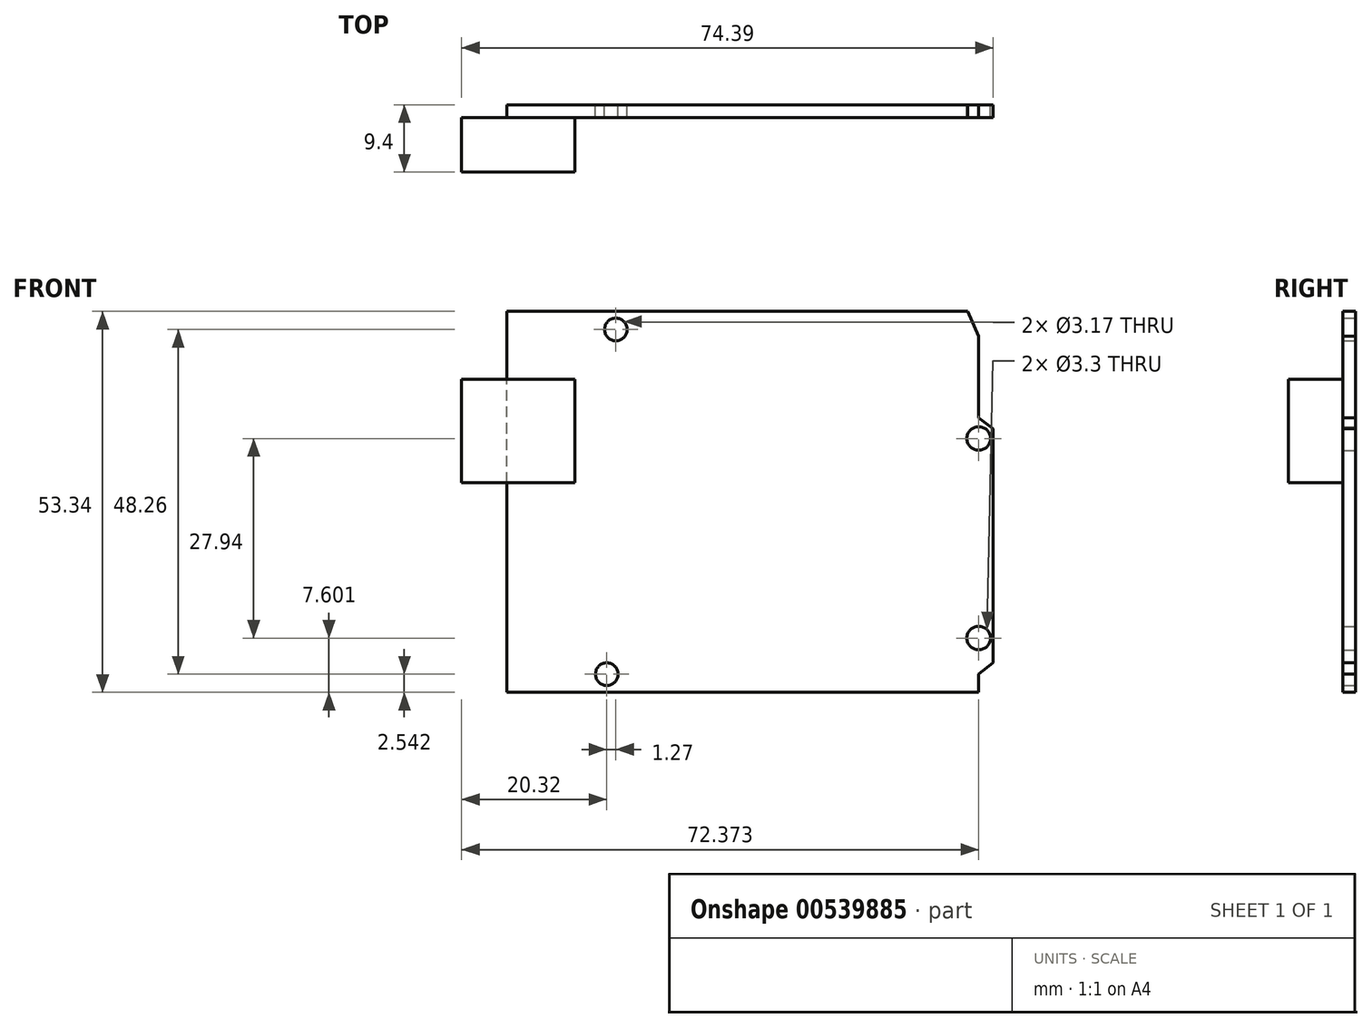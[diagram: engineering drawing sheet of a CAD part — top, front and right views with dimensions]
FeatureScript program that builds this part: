
annotation { "Feature Type Name" : "Feature", "Feature Type Description" : "" }
export const myFeature = defineFeature(function(context is Context, id is Id, definition is map)
    precondition{}
    {
        {
            var Q0;
            Q0=qCreatedBy(makeId("Front.planeOp"),FACE);
            var sketch = newSketch(context, id + "F0", { "sketchPlane" : qUnion([Q0])});
            skLineSegment(sketch, "E0", {"start": v(-50.8, -29.33) * mm, "end": v(-50.8, 24.01) * mm});
            skLineSegment(sketch, "E1", {"start": v(-50.8, -29.33) * mm, "end": v(15.24, -29.33) * mm});
            skLineSegment(sketch, "E2", {"start": v(15.24, -29.33) * mm, "end": v(15.24, -26.79) * mm});
            skLineSegment(sketch, "E3", {"start": v(15.24, -26.79) * mm, "end": v(17.24, -25.22) * mm});
            skLineSegment(sketch, "E4", {"start": v(17.24, -25.22) * mm, "end": v(17.24, 7.55) * mm});
            skLineSegment(sketch, "E5", {"start": v(17.24, 7.55) * mm, "end": v(15.24, 9.12) * mm});
            skLineSegment(sketch, "E6", {"start": v(-50.8, 24.01) * mm, "end": v(13.72, 24.01) * mm});
            skLineSegment(sketch, "E7", {"start": v(15.24, 9.12) * mm, "end": v(15.24, 20.55) * mm});
            skLineSegment(sketch, "E8", {"start": v(15.24, 20.55) * mm, "end": v(13.72, 24.01) * mm});
            skLineSegment(sketch, "E9", {"start": v(-50.8, 24.01) * mm, "end": v(-35.56, 24.01) * mm});
            skLineSegment(sketch, "E10", {"start": v(-35.56, 24.01) * mm, "end": v(-35.56, 21.47) * mm});
            skCircle(sketch, "E11", {"center": v(-35.56, 21.47) * mm, "radius": 1.59 * mm});
            skLineSegment(sketch, "E12", {"start": v(-50.8, -29.33) * mm, "end": v(-36.83, -29.33) * mm});
            skLineSegment(sketch, "E13", {"start": v(-36.83, -29.33) * mm, "end": v(-36.83, -26.79) * mm});
            skCircle(sketch, "E14", {"center": v(-36.83, -26.79) * mm, "radius": 1.59 * mm});
            skLineSegment(sketch, "E15", {"start": v(-50.8, -29.33) * mm, "end": v(0, -29.33) * mm});
            skSolve(sketch);
        }
        {
            var Q0;
            {var subQ0=sQuery(id+"F0.wireOp",EDGE,"E0");Q0=makeQuery(id+"F0.imprint","IMPRINT",FACE,{"disambiguationData":[TD([[makeQuery(id+"F0.imprint","IMPRINT",EDGE,{"derivedFrom":subQ0}),-1.0]])]});}
            var sketch = newSketch(context, id + "F1", { "sketchPlane" : qUnion([Q0])});
            skLineSegment(sketch, "E16", {"start": v(15.22, -29.35) * mm, "end": v(15.22, -21.73) * mm});
            skCircle(sketch, "E17", {"center": v(15.22, -21.73) * mm, "radius": 1.59 * mm});
            skLineSegment(sketch, "E18", {"start": v(15.22, -29.35) * mm, "end": v(15.22, 6.21) * mm});
            skCircle(sketch, "E19", {"center": v(15.22, 6.21) * mm, "radius": 1.59 * mm});
            skSolve(sketch);
        }
        {
            var Q0;
            {var subQ0=sQuery(id+"F0.wireOp",EDGE,"E0");Q0=makeQuery(id+"F0.imprint","IMPRINT",FACE,{"disambiguationData":[TD([[makeQuery(id+"F0.imprint","IMPRINT",EDGE,{"derivedFrom":subQ0}),-1.0]])]});}
            extrude(context, id + "F2", {"entities" : qUnion([Q0]), "depth" : 1.78 * mm, "offsetDistance" : 25.4 * mm});
        }
        {
            var Q0;
            Q0=sQuery(id+"F1.wireOp",VERTEX,"E17.center");
            var Q1;
            Q1=sQuery(id+"F1.wireOp",VERTEX,"E19.center");
            var Q2;
            Q2=makeQuery(id+"F2.opExtrude","SWEPT_BODY",BODY,{"disambiguationData":[OSD([sQuery(id+"F0.wireOp",EDGE,"E0"),sQuery(id+"F0.wireOp",EDGE,"E2"),sQuery(id+"F0.wireOp",EDGE,"E3"),sQuery(id+"F0.wireOp",EDGE,"E4"),sQuery(id+"F0.wireOp",EDGE,"E5"),sQuery(id+"F0.wireOp",EDGE,"E6"),sQuery(id+"F0.wireOp",EDGE,"E7"),sQuery(id+"F0.wireOp",EDGE,"E8"),sQuery(id+"F0.wireOp",EDGE,"E9"),sQuery(id+"F0.wireOp",EDGE,"E11"),sQuery(id+"F0.wireOp",EDGE,"E14"),sQuery(id+"F0.wireOp",EDGE,"E1")])]});
            hole(context, id + "F3", {"style" : HoleStyle.SIMPLE, "endStyle" : HoleEndStyle.THROUGH, "oppositeDirection" : true, "holeDiameter" : 3.3 * mm, "isTappedThrough" : true, "tappedDepth" : 12.7 * mm, "tapClearance" : 3, "locations" : qUnion([Q0, Q1]), "scope" : qUnion([Q2])});
        }
        {
            var Q0;
            Q0=makeQuery(id+"F2.opExtrude","CAP_FACE",FACE,{"disambiguationData":[OSD([sQuery(id+"F0.wireOp",EDGE,"E0"),sQuery(id+"F0.wireOp",EDGE,"E2"),sQuery(id+"F0.wireOp",EDGE,"E3"),sQuery(id+"F0.wireOp",EDGE,"E4"),sQuery(id+"F0.wireOp",EDGE,"E5"),sQuery(id+"F0.wireOp",EDGE,"E6"),sQuery(id+"F0.wireOp",EDGE,"E7"),sQuery(id+"F0.wireOp",EDGE,"E8"),sQuery(id+"F0.wireOp",EDGE,"E9"),sQuery(id+"F0.wireOp",EDGE,"E11"),sQuery(id+"F0.wireOp",EDGE,"E14"),sQuery(id+"F0.wireOp",EDGE,"E1")])],"isStart":false});
            var sketch = newSketch(context, id + "F4", { "sketchPlane" : qUnion([Q0])});
            skLineSegment(sketch, "E20", {"start": v(-50.8, -29.33) * mm, "end": v(-50.8, 14.49) * mm});
            skLineSegment(sketch, "E21", {"start": v(-50.8, 14.49) * mm, "end": v(-57.15, 14.49) * mm});
            skLineSegment(sketch, "E22", {"start": v(-57.15, 14.49) * mm, "end": v(-57.15, 0) * mm});
            skLineSegment(sketch, "E23", {"start": v(-50.8, 14.49) * mm, "end": v(-41.28, 14.49) * mm});
            skLineSegment(sketch, "E24", {"start": v(-41.28, 14.49) * mm, "end": v(-41.28, 0) * mm});
            skLineSegment(sketch, "E25", {"start": v(-41.28, 0) * mm, "end": v(-57.15, 0) * mm});
            skLineSegment(sketch, "E26", {"start": v(-50.8, -29.33) * mm, "end": v(-50.8, -26.15) * mm});
            skLineSegment(sketch, "E27", {"start": v(-50.8, -26.15) * mm, "end": v(-50.8, -18.53) * mm});
            skLineSegment(sketch, "E28", {"start": v(-50.8, -18.53) * mm, "end": v(-52.7, -18.53) * mm});
            skLineSegment(sketch, "E29", {"start": v(-52.7, -18.53) * mm, "end": v(-52.7, -26.15) * mm});
            skLineSegment(sketch, "E30", {"start": v(-50.8, -18.53) * mm, "end": v(-39.37, -18.53) * mm});
            skLineSegment(sketch, "E31", {"start": v(-39.37, -18.53) * mm, "end": v(-39.37, -26.15) * mm});
            skLineSegment(sketch, "E32", {"start": v(-39.37, -26.15) * mm, "end": v(-52.7, -26.15) * mm});
            skSolve(sketch);
        }
        {
            var Q0;
            {var subQ0=sQuery(id+"F4.wireOp",EDGE,"E21");Q0=makeQuery(id+"F4.imprint","IMPRINT",FACE,{"disambiguationData":[TD([[makeQuery(id+"F4.imprint","IMPRINT",EDGE,{"derivedFrom":subQ0}),1.0]])]});}
            var Q1;
            {var subQ0=sQuery(id+"F4.wireOp",EDGE,"E23");Q1=makeQuery(id+"F4.imprint","IMPRINT",FACE,{"disambiguationData":[TD([[makeQuery(id+"F4.imprint","IMPRINT",EDGE,{"derivedFrom":subQ0}),-1.0]])]});}
            var Q2;
            {var subQ0=sQuery(id+"F4.wireOp",EDGE,"E27");Q2=makeQuery(id+"F4.imprint","IMPRINT",FACE,{"disambiguationData":[TD([[makeQuery(id+"F4.imprint","IMPRINT",EDGE,{"derivedFrom":subQ0}),-1.0]])]});}
            var Q3;
            {var subQ0=sQuery(id+"F4.wireOp",EDGE,"E27");Q3=makeQuery(id+"F4.imprint","IMPRINT",FACE,{"disambiguationData":[TD([[makeQuery(id+"F4.imprint","IMPRINT",EDGE,{"derivedFrom":subQ0}),1.0]])]});}
            extrude(context, id + "F5", {"entities" : qUnion([Q0, Q1, Q2, Q3]), "operationType" : NewBodyOperationType.ADD, "depth" : 7.62 * mm, "offsetDistance" : 25.4 * mm});
        }
    });
